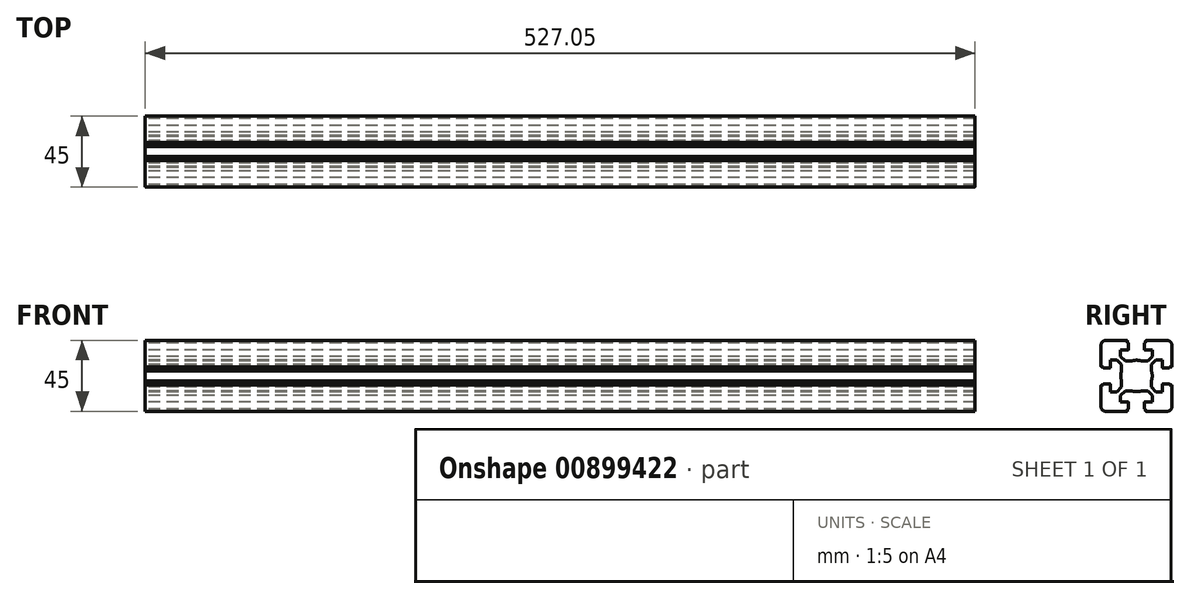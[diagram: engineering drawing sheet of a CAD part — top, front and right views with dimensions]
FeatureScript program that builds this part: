
annotation { "Feature Type Name" : "Feature", "Feature Type Description" : "" }
export const myFeature = defineFeature(function(context is Context, id is Id, definition is map)
    precondition{}
    {
        {
            var Q0;
            Q0=qCreatedBy(makeId("Right.planeOp"),FACE);
            var sketch = newSketch(context, id + "F0", { "sketchPlane" : qUnion([Q0])});
            skLineSegment(sketch, "E0", {"start": v(-20.09, -10.29) * mm, "end": v(-21.29, -10.29) * mm});
            skArc(sketch, "E1", {"start": v(-21.29, -10.29) * mm, "mid": v(-21.5, -10.38) * mm, "end": v(-21.59, -10.59) * mm});
            skLineSegment(sketch, "E2", {"start": v(-21.59, -10.59) * mm, "end": v(-21.59, -23.99) * mm});
            skArc(sketch, "E3", {"start": v(-21.59, -23.99) * mm, "mid": v(-20.7, -26.11) * mm, "end": v(-18.59, -26.99) * mm});
            skLineSegment(sketch, "E4", {"start": v(-18.59, -26.99) * mm, "end": v(-5.19, -26.99) * mm});
            skArc(sketch, "E5", {"start": v(-5.19, -26.99) * mm, "mid": v(-4.98, -26.9) * mm, "end": v(-4.89, -26.69) * mm});
            skLineSegment(sketch, "E6", {"start": v(-4.89, -26.69) * mm, "end": v(-4.89, -25.49) * mm});
            skLineSegment(sketch, "E7", {"start": v(-4.89, -25.49) * mm, "end": v(-4.39, -25.49) * mm});
            skArc(sketch, "E8", {"start": v(-4.39, -25.49) * mm, "mid": v(-4.18, -25.4) * mm, "end": v(-4.09, -25.19) * mm});
            skLineSegment(sketch, "E9", {"start": v(-4.09, -25.19) * mm, "end": v(-4.09, -21.29) * mm});
            skArc(sketch, "E10", {"start": v(-4.09, -21.29) * mm, "mid": v(-4.18, -21.08) * mm, "end": v(-4.39, -20.99) * mm});
            skLineSegment(sketch, "E11", {"start": v(-4.39, -20.99) * mm, "end": v(-9.14, -20.99) * mm});
            skLineSegment(sketch, "E12", {"start": v(-9.14, -20.99) * mm, "end": v(-9.14, -16.88) * mm});
            skLineSegment(sketch, "E13", {"start": v(-9.14, -16.88) * mm, "end": v(-6.25, -13.99) * mm});
            skLineSegment(sketch, "E14", {"start": v(-6.25, -13.99) * mm, "end": v(-2.21, -13.99) * mm});
            skArc(sketch, "E15", {"start": v(-2.21, -13.99) * mm, "mid": v(0.91, -14.49) * mm, "end": v(4.03, -13.99) * mm});
            skLineSegment(sketch, "E16", {"start": v(-20.09, -10.29) * mm, "end": v(-20.09, -9.79) * mm});
            skArc(sketch, "E17", {"start": v(-20.09, -9.79) * mm, "mid": v(-20, -9.58) * mm, "end": v(-19.79, -9.49) * mm});
            skLineSegment(sketch, "E18", {"start": v(-19.79, -9.49) * mm, "end": v(-15.89, -9.49) * mm});
            skArc(sketch, "E19", {"start": v(-15.89, -9.49) * mm, "mid": v(-15.68, -9.58) * mm, "end": v(-15.59, -9.79) * mm});
            skLineSegment(sketch, "E20", {"start": v(-15.59, -9.79) * mm, "end": v(-15.59, -14.54) * mm});
            skLineSegment(sketch, "E21", {"start": v(-15.59, -14.54) * mm, "end": v(-11.48, -14.54) * mm});
            skLineSegment(sketch, "E22", {"start": v(-11.48, -14.54) * mm, "end": v(-8.59, -11.65) * mm});
            skLineSegment(sketch, "E23", {"start": v(-8.59, -11.65) * mm, "end": v(-8.59, -7.61) * mm});
            skLineSegment(sketch, "E24", {"start": v(29.82, -4.49) * mm, "end": v(-31.05, -4.49) * mm});
            skLineSegment(sketch, "E25.MirrorCS", {"start": v(6.71, -25.49) * mm, "end": v(6.21, -25.49) * mm});
            skArc(sketch, "E26.MirrorCS", {"start": v(7.01, -26.99) * mm, "mid": v(6.8, -26.9) * mm, "end": v(6.71, -26.69) * mm});
            skLineSegment(sketch, "E27.MirrorCS", {"start": v(10.41, -11.65) * mm, "end": v(10.41, -7.61) * mm});
            skArc(sketch, "E28.MirrorCS", {"start": v(6.21, -25.49) * mm, "mid": v(6, -25.4) * mm, "end": v(5.91, -25.19) * mm});
            skLineSegment(sketch, "E29.MirrorCS", {"start": v(6.71, -26.69) * mm, "end": v(6.71, -25.49) * mm});
            skArc(sketch, "E30.MirrorCS", {"start": v(5.91, -21.29) * mm, "mid": v(6, -21.08) * mm, "end": v(6.21, -20.99) * mm});
            skLineSegment(sketch, "E31.MirrorCS", {"start": v(10.96, -16.88) * mm, "end": v(8.07, -13.99) * mm});
            skLineSegment(sketch, "E32.MirrorCS", {"start": v(13.3, -14.54) * mm, "end": v(10.41, -11.65) * mm});
            skLineSegment(sketch, "E33.MirrorCS", {"start": v(17.41, -14.54) * mm, "end": v(13.3, -14.54) * mm});
            skLineSegment(sketch, "E34.MirrorCS", {"start": v(17.41, -9.79) * mm, "end": v(17.41, -14.54) * mm});
            skLineSegment(sketch, "E35.MirrorCS", {"start": v(6.21, -20.99) * mm, "end": v(10.96, -20.99) * mm});
            skLineSegment(sketch, "E36.MirrorCS", {"start": v(8.07, -13.99) * mm, "end": v(4.03, -13.99) * mm});
            skArc(sketch, "E37.MirrorCS", {"start": v(4.03, -13.99) * mm, "mid": v(0.91, -14.49) * mm, "end": v(-2.21, -13.99) * mm});
            skLineSegment(sketch, "E38.MirrorCS", {"start": v(10.96, -20.99) * mm, "end": v(10.96, -16.88) * mm});
            skLineSegment(sketch, "E39.MirrorCS", {"start": v(5.91, -25.19) * mm, "end": v(5.91, -21.29) * mm});
            skArc(sketch, "E40.MirrorCS", {"start": v(23.41, -23.99) * mm, "mid": v(22.53, -26.11) * mm, "end": v(20.41, -26.99) * mm});
            skLineSegment(sketch, "E41.MirrorCS", {"start": v(20.41, -26.99) * mm, "end": v(7.01, -26.99) * mm});
            skLineSegment(sketch, "E42.MirrorCS", {"start": v(23.41, -10.59) * mm, "end": v(23.41, -23.99) * mm});
            skArc(sketch, "E43.MirrorCS", {"start": v(17.71, -9.49) * mm, "mid": v(17.5, -9.58) * mm, "end": v(17.41, -9.79) * mm});
            skArc(sketch, "E44.MirrorCS", {"start": v(23.11, -10.29) * mm, "mid": v(23.32, -10.38) * mm, "end": v(23.41, -10.59) * mm});
            skLineSegment(sketch, "E45.MirrorCS", {"start": v(21.91, -10.29) * mm, "end": v(21.91, -9.79) * mm});
            skLineSegment(sketch, "E46.MirrorCS", {"start": v(21.91, -10.29) * mm, "end": v(23.11, -10.29) * mm});
            skArc(sketch, "E47.MirrorCS", {"start": v(21.91, -9.79) * mm, "mid": v(21.82, -9.58) * mm, "end": v(21.61, -9.49) * mm});
            skLineSegment(sketch, "E48.MirrorCS", {"start": v(21.61, -9.49) * mm, "end": v(17.71, -9.49) * mm});
            skLineSegment(sketch, "E49.MirrorCS", {"start": v(6.71, 16.51) * mm, "end": v(6.21, 16.51) * mm});
            skArc(sketch, "E50.MirrorCS", {"start": v(-4.39, 16.51) * mm, "mid": v(-4.18, 16.42) * mm, "end": v(-4.09, 16.21) * mm});
            skLineSegment(sketch, "E51.MirrorCS", {"start": v(-4.89, 16.51) * mm, "end": v(-4.39, 16.51) * mm});
            skArc(sketch, "E52.MirrorCS", {"start": v(5.91, 12.31) * mm, "mid": v(6, 12.1) * mm, "end": v(6.21, 12.01) * mm});
            skLineSegment(sketch, "E53.MirrorCS", {"start": v(6.71, 17.71) * mm, "end": v(6.71, 16.51) * mm});
            skLineSegment(sketch, "E54.MirrorCS", {"start": v(-4.89, 17.71) * mm, "end": v(-4.89, 16.51) * mm});
            skArc(sketch, "E55.MirrorCS", {"start": v(-5.19, 18.01) * mm, "mid": v(-4.98, 17.92) * mm, "end": v(-4.89, 17.71) * mm});
            skArc(sketch, "E56.MirrorCS", {"start": v(-4.09, 12.31) * mm, "mid": v(-4.18, 12.1) * mm, "end": v(-4.39, 12.01) * mm});
            skArc(sketch, "E57.MirrorCS", {"start": v(7.01, 18.01) * mm, "mid": v(6.8, 17.92) * mm, "end": v(6.71, 17.71) * mm});
            skArc(sketch, "E58.MirrorCS", {"start": v(6.21, 16.51) * mm, "mid": v(6, 16.42) * mm, "end": v(5.91, 16.21) * mm});
            skArc(sketch, "E59.MirrorCS", {"start": v(23.11, 1.31) * mm, "mid": v(23.32, 1.4) * mm, "end": v(23.41, 1.61) * mm});
            skLineSegment(sketch, "E60.MirrorCS", {"start": v(21.91, 1.31) * mm, "end": v(21.91, 0.81) * mm});
            skArc(sketch, "E61.MirrorCS", {"start": v(-15.89, 0.51) * mm, "mid": v(-15.68, 0.6) * mm, "end": v(-15.59, 0.81) * mm});
            skArc(sketch, "E62.MirrorCS", {"start": v(-21.29, 1.31) * mm, "mid": v(-21.5, 1.4) * mm, "end": v(-21.59, 1.61) * mm});
            skArc(sketch, "E63.MirrorCS", {"start": v(17.71, 0.51) * mm, "mid": v(17.5, 0.6) * mm, "end": v(17.41, 0.81) * mm});
            skArc(sketch, "E64.MirrorCS", {"start": v(21.91, 0.81) * mm, "mid": v(21.82, 0.6) * mm, "end": v(21.61, 0.51) * mm});
            skLineSegment(sketch, "E65.MirrorCS", {"start": v(21.91, 1.31) * mm, "end": v(23.11, 1.31) * mm});
            skArc(sketch, "E66.MirrorCS", {"start": v(14.31, 5.31) * mm, "mid": v(14.1, 5.4) * mm, "end": v(14.01, 5.61) * mm});
            skArc(sketch, "E67.MirrorCS", {"start": v(-20.09, 0.81) * mm, "mid": v(-20, 0.6) * mm, "end": v(-19.79, 0.51) * mm});
            skLineSegment(sketch, "E68.MirrorCS", {"start": v(-20.09, 1.31) * mm, "end": v(-21.29, 1.31) * mm});
            skLineSegment(sketch, "E69.MirrorCS", {"start": v(-20.09, 1.31) * mm, "end": v(-20.09, 0.81) * mm});
            skLineSegment(sketch, "E70.MirrorCS", {"start": v(8.07, 5.01) * mm, "end": v(4.03, 5.01) * mm});
            skLineSegment(sketch, "E71.MirrorCS", {"start": v(-4.09, 16.21) * mm, "end": v(-4.09, 12.31) * mm});
            skLineSegment(sketch, "E72.MirrorCS", {"start": v(-9.14, 12.01) * mm, "end": v(-9.14, 7.9) * mm});
            skLineSegment(sketch, "E73.MirrorCS", {"start": v(-15.59, 5.56) * mm, "end": v(-11.48, 5.56) * mm});
            skLineSegment(sketch, "E74.MirrorCS", {"start": v(-4.39, 12.01) * mm, "end": v(-9.14, 12.01) * mm});
            skLineSegment(sketch, "E75.MirrorCS", {"start": v(-9.14, 7.9) * mm, "end": v(-6.25, 5.01) * mm});
            skLineSegment(sketch, "E76.MirrorCS", {"start": v(10.96, 12.01) * mm, "end": v(10.96, 7.9) * mm});
            skArc(sketch, "E77.MirrorCS", {"start": v(-21.59, 15.01) * mm, "mid": v(-20.7, 17.13) * mm, "end": v(-18.59, 18.01) * mm});
            skLineSegment(sketch, "E78.MirrorCS", {"start": v(23.41, 1.61) * mm, "end": v(23.41, 15.01) * mm});
            skLineSegment(sketch, "E79.MirrorCS", {"start": v(13.3, 5.56) * mm, "end": v(10.41, 2.67) * mm});
            skLineSegment(sketch, "E80.MirrorCS", {"start": v(-8.59, 2.67) * mm, "end": v(-8.59, -1.37) * mm});
            skLineSegment(sketch, "E81.MirrorCS", {"start": v(-15.59, 0.81) * mm, "end": v(-15.59, 5.56) * mm});
            skLineSegment(sketch, "E82.MirrorCS", {"start": v(10.41, 2.67) * mm, "end": v(10.41, -1.37) * mm});
            skLineSegment(sketch, "E83.MirrorCS", {"start": v(-18.59, 18.01) * mm, "end": v(-5.19, 18.01) * mm});
            skLineSegment(sketch, "E84.MirrorCS", {"start": v(10.96, 7.9) * mm, "end": v(8.07, 5.01) * mm});
            skLineSegment(sketch, "E85.MirrorCS", {"start": v(17.41, 5.56) * mm, "end": v(13.3, 5.56) * mm});
            skArc(sketch, "E86.MirrorCS", {"start": v(23.41, 15.01) * mm, "mid": v(22.53, 17.13) * mm, "end": v(20.41, 18.01) * mm});
            skLineSegment(sketch, "E87.MirrorCS", {"start": v(5.91, 16.21) * mm, "end": v(5.91, 12.31) * mm});
            skLineSegment(sketch, "E88.MirrorCS", {"start": v(17.41, 0.81) * mm, "end": v(17.41, 5.56) * mm});
            skLineSegment(sketch, "E89.MirrorCS", {"start": v(-11.48, 5.56) * mm, "end": v(-8.59, 2.67) * mm});
            skLineSegment(sketch, "E90.MirrorCS", {"start": v(-6.25, 5.01) * mm, "end": v(-2.21, 5.01) * mm});
            skLineSegment(sketch, "E91.MirrorCS", {"start": v(-21.59, 1.61) * mm, "end": v(-21.59, 15.01) * mm});
            skArc(sketch, "E92.MirrorCS", {"start": v(4.03, 5.01) * mm, "mid": v(0.91, 5.51) * mm, "end": v(-2.21, 5.01) * mm});
            skLineSegment(sketch, "E93.MirrorCS", {"start": v(6.21, 12.01) * mm, "end": v(10.96, 12.01) * mm});
            skArc(sketch, "E94.MirrorCS", {"start": v(-2.21, 5.01) * mm, "mid": v(0.91, 5.51) * mm, "end": v(4.03, 5.01) * mm});
            skLineSegment(sketch, "E95.MirrorCS", {"start": v(20.41, 18.01) * mm, "end": v(7.01, 18.01) * mm});
            skLineSegment(sketch, "E96.MirrorCS", {"start": v(-19.79, 0.51) * mm, "end": v(-15.89, 0.51) * mm});
            skLineSegment(sketch, "E97.MirrorCS", {"start": v(21.61, 0.51) * mm, "end": v(17.71, 0.51) * mm});
            skLineSegment(sketch, "E98.MirrorCS", {"start": v(0.91, -27.65) * mm, "end": v(0.91, 19.82) * mm});
            skArc(sketch, "E99", {"start": v(-8.59, -1.37) * mm, "mid": v(-9.09, -4.49) * mm, "end": v(-8.59, -7.61) * mm});
            skArc(sketch, "E100", {"start": v(10.41, -7.61) * mm, "mid": v(10.91, -4.49) * mm, "end": v(10.41, -1.37) * mm});
            skSolve(sketch);
        }
        {
            var Q0;
            Q0=qSketchRegion(id+"F0",true);
            extrude(context, id + "F1", {"entities" : qUnion([Q0]), "depth" : 527.05 * mm, "offsetDistance" : 25.4 * mm});
        }
    });
